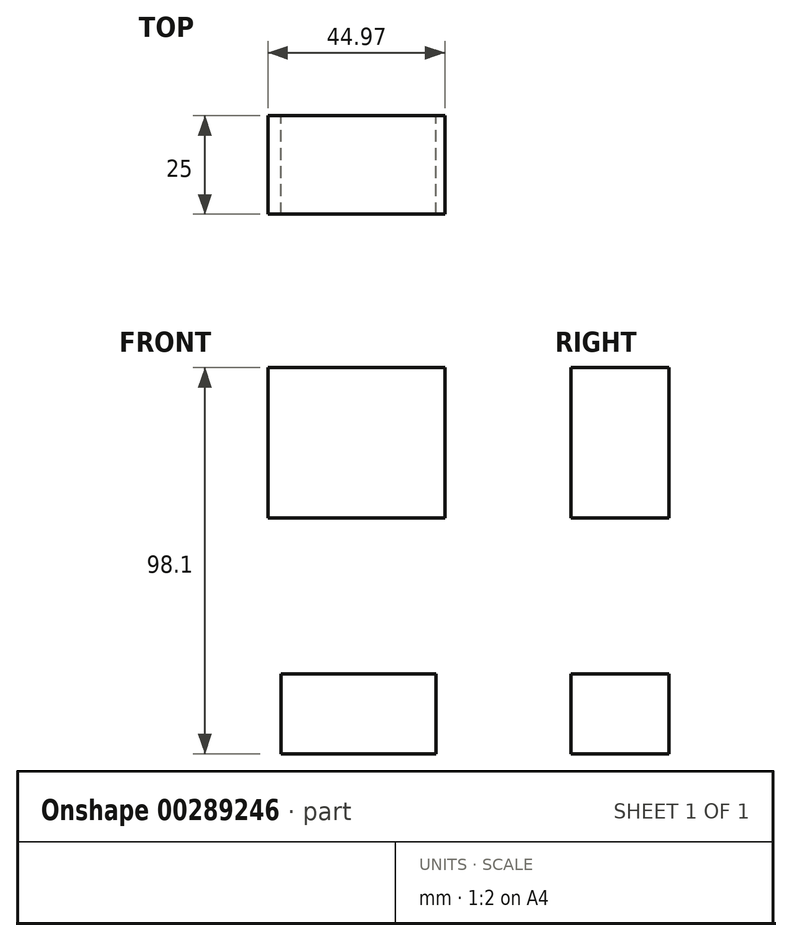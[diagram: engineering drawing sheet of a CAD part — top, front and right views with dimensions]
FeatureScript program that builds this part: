
annotation { "Feature Type Name" : "Feature", "Feature Type Description" : "" }
export const myFeature = defineFeature(function(context is Context, id is Id, definition is map)
    precondition{}
    {
        {
            var Q0;
            Q0=qCreatedBy(makeId("Front.planeOp"),FACE);
            var sketch = newSketch(context, id + "F0", { "sketchPlane" : qUnion([Q0])});
            skLineSegment(sketch, "E0.bottom", {"start": v(-102.87, 32.32) * mm, "end": v(-57.9, 32.32) * mm});
            skLineSegment(sketch, "E0.top", {"start": v(-102.87, 70.55) * mm, "end": v(-57.9, 70.55) * mm});
            skLineSegment(sketch, "E0.left", {"start": v(-102.87, 32.32) * mm, "end": v(-102.87, 70.55) * mm});
            skLineSegment(sketch, "E0.right", {"start": v(-57.9, 32.32) * mm, "end": v(-57.9, 70.55) * mm});
            skPoint(sketch, "E0.middle", {"position": v(-80.39, 51.44) * mm});
            skLineSegment(sketch, "E1.bottom", {"start": v(-99.5, -27.55) * mm, "end": v(-60.15, -27.55) * mm});
            skLineSegment(sketch, "E1.top", {"start": v(-99.5, -7.3) * mm, "end": v(-60.15, -7.3) * mm});
            skLineSegment(sketch, "E1.left", {"start": v(-99.5, -27.55) * mm, "end": v(-99.5, -7.3) * mm});
            skLineSegment(sketch, "E1.right", {"start": v(-60.15, -27.55) * mm, "end": v(-60.15, -7.3) * mm});
            skPoint(sketch, "E1.middle", {"position": v(-79.83, -17.43) * mm});
            skSolve(sketch);
        }
        {
            var Q0;
            Q0=makeQuery(id+"F0.imprint","IMPRINT",FACE,{"disambiguationData":[TD([[makeQuery(id+"F0.imprint","IMPRINT",EDGE,{"derivedFrom":sQuery(id+"F0.wireOp",EDGE,"E0.bottom")}),1.0]])]});
            var Q1;
            Q1=makeQuery(id+"F0.imprint","IMPRINT",FACE,{"disambiguationData":[TD([[makeQuery(id+"F0.imprint","IMPRINT",EDGE,{"derivedFrom":sQuery(id+"F0.wireOp",EDGE,"E1.bottom")}),1.0]])]});
            extrude(context, id + "F1", {"entities" : qUnion([Q0, Q1]), "depth" : 25 * mm});
        }
    });
